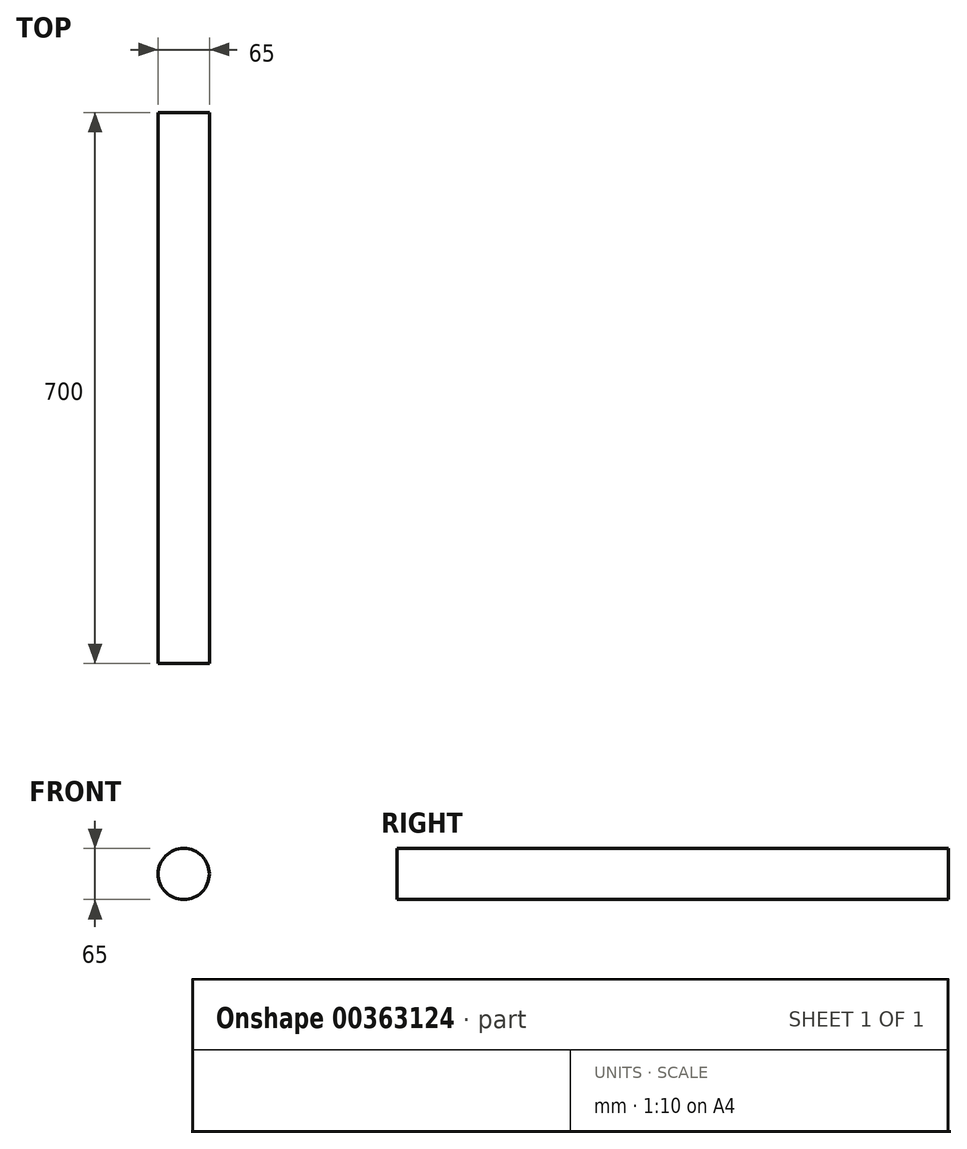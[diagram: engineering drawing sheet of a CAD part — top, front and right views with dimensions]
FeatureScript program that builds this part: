
annotation { "Feature Type Name" : "Feature", "Feature Type Description" : "" }
export const myFeature = defineFeature(function(context is Context, id is Id, definition is map)
    precondition{}
    {
        {
            var Q0;
            Q0=qCreatedBy(makeId("Front.planeOp"),FACE);
            var sketch = newSketch(context, id + "F0", { "sketchPlane" : qUnion([Q0])});
            skCircle(sketch, "E0", {"center": v(0, 0) * mm, "radius": 32.5 * mm});
            skSolve(sketch);
        }
        {
            var Q0;
            Q0 = qSketchRegion(id + "F0", true);
            extrude(context, id + "F1", {"entities" : qUnion([Q0]), "depth" : 700 * mm});
        }
    });
